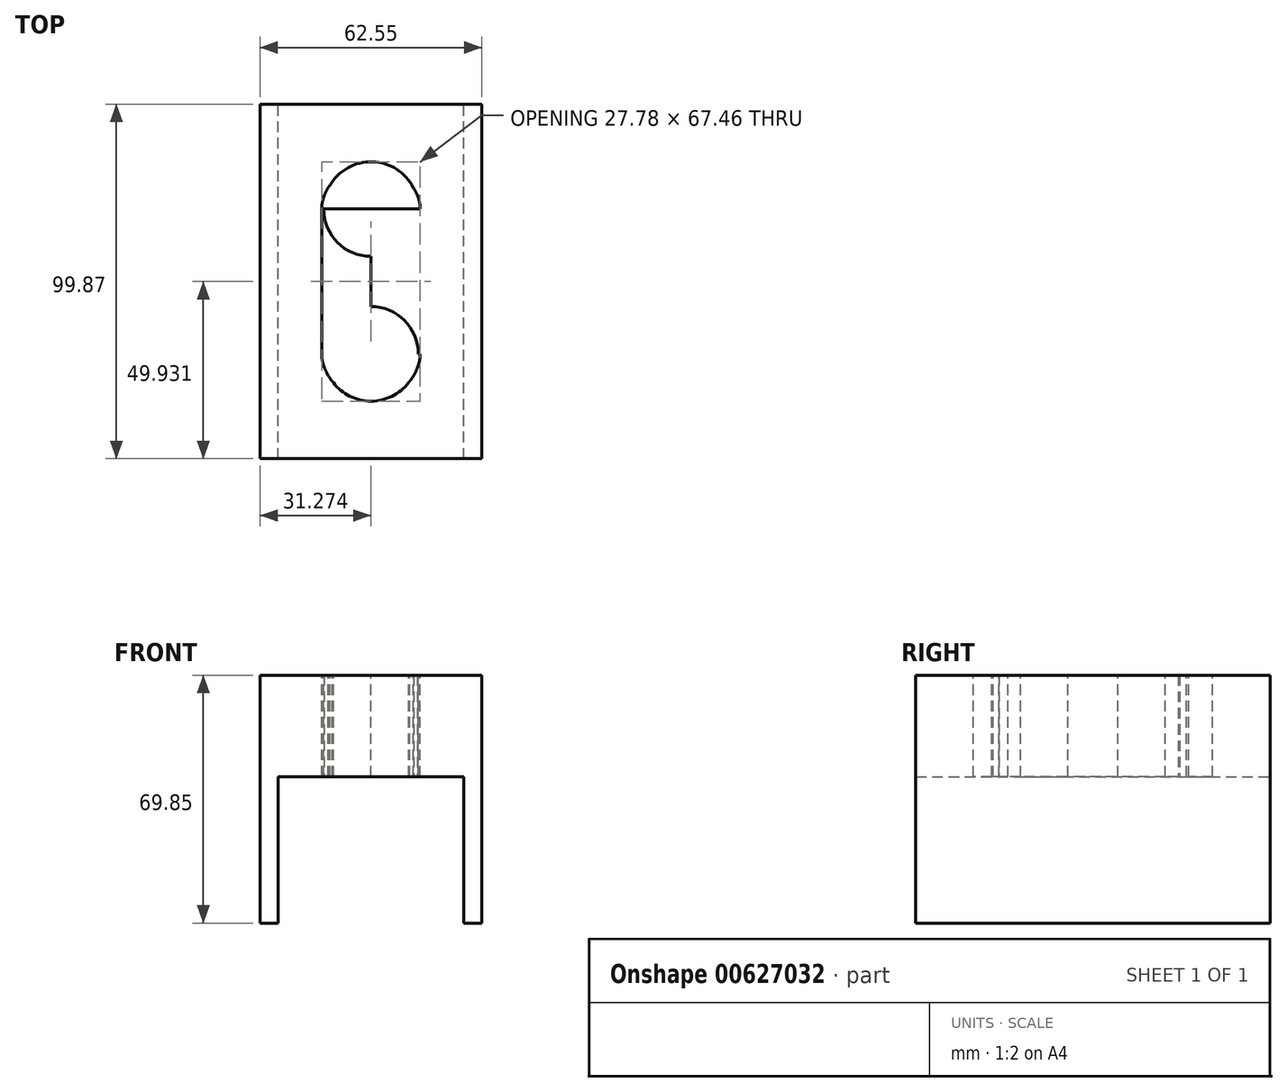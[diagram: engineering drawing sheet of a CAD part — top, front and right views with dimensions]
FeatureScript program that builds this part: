
annotation { "Feature Type Name" : "Feature", "Feature Type Description" : "" }
export const myFeature = defineFeature(function(context is Context, id is Id, definition is map)
    precondition{}
    {
        {
            var Q0;
            Q0=qCreatedBy(makeId("Front.planeOp"),FACE);
            var sketch = newSketch(context, id + "F0", { "sketchPlane" : qUnion([Q0])});
            skLineSegment(sketch, "E0", {"start": v(-13.71, -48.82) * mm, "end": v(-13.71, 21.03) * mm});
            skLineSegment(sketch, "E1", {"start": v(-13.71, 21.03) * mm, "end": v(48.84, 21.03) * mm});
            skLineSegment(sketch, "E2", {"start": v(48.84, 21.03) * mm, "end": v(48.84, -48.82) * mm});
            skLineSegment(sketch, "E3", {"start": v(-13.71, -48.82) * mm, "end": v(-8.63, -48.82) * mm});
            skLineSegment(sketch, "E4", {"start": v(-8.63, -48.82) * mm, "end": v(-8.63, -7.55) * mm});
            skLineSegment(sketch, "E5", {"start": v(-8.63, -7.55) * mm, "end": v(43.76, -7.55) * mm});
            skLineSegment(sketch, "E6", {"start": v(43.76, -7.55) * mm, "end": v(43.76, -48.82) * mm});
            skLineSegment(sketch, "E7", {"start": v(43.76, -48.82) * mm, "end": v(48.84, -48.82) * mm});
            skSolve(sketch);
        }
        {
            var Q0;
            Q0=makeQuery(id+"F0.imprint","IMPRINT",FACE,{"disambiguationData":[TD([[makeQuery(id+"F0.imprint","IMPRINT",EDGE,{"derivedFrom":sQuery(id+"F0.wireOp",EDGE,"E0")}),-1.0]])]});
            extrude(context, id + "F1", {"entities" : qUnion([Q0]), "depth" : 99.87 * mm, "offsetDistance" : 25.4 * mm});
        }
        {
            var Q0;
            Q0=makeQuery(id+"F1.opExtrude","SWEPT_FACE",FACE,{"disambiguationData":[OSD([sQuery(id+"F0.wireOp",EDGE,"E1")])]});
            var sketch = newSketch(context, id + "F2", { "sketchPlane" : qUnion([Q0])});
            skLineSegment(sketch, "E8", {"start": v(17.56, -49.94) * mm, "end": v(17.56, -29.54) * mm});
            skPoint(sketch, "E8.startSnap0", {"position": v(17.56, 0) * mm});
            skPoint(sketch, "E8.startSnap1", {"position": v(48.84, -49.94) * mm});
            skLineSegment(sketch, "E9", {"start": v(17.56, -49.94) * mm, "end": v(17.56, -70.34) * mm});
            skCircle(sketch, "E10", {"center": v(17.56, -70.34) * mm, "radius": 13.34 * mm});
            skLineSegment(sketch, "E11", {"start": v(17.56, -29.54) * mm, "end": v(3.67, -29.54) * mm});
            skLineSegment(sketch, "E12", {"start": v(17.56, -29.54) * mm, "end": v(31.45, -29.54) * mm});
            skLineSegment(sketch, "E13.MirrorCS", {"start": v(31.65, -49.94) * mm, "end": v(17.56, -49.94) * mm});
            skLineSegment(sketch, "E14.MirrorCS", {"start": v(17.56, -49.94) * mm, "end": v(17.56, -68.43) * mm});
            skLineSegment(sketch, "E15", {"start": v(17.56, -49.94) * mm, "end": v(17.56, -29.3) * mm});
            skLineSegment(sketch, "E16", {"start": v(31.45, -70.34) * mm, "end": v(31.45, -71.45) * mm});
            skLineSegment(sketch, "E17", {"start": v(17.56, -70.34) * mm, "end": v(31.45, -70.34) * mm});
            skLineSegment(sketch, "E18", {"start": v(31.45, -29.54) * mm, "end": v(31.45, -70.34) * mm});
            skLineSegment(sketch, "E19.MirrorCS", {"start": v(3.67, -29.54) * mm, "end": v(3.67, -70.34) * mm});
            skCircle(sketch, "E20.MirrorC", {"center": v(17.56, -29.54) * mm, "radius": 13.34 * mm});
            skArc(sketch, "E21", {"start": v(31.45, -29.54) * mm, "mid": v(30.95, -26.4) * mm, "end": v(29.5, -23.6) * mm});
            skFitSpline(sketch, "E22", {"points": [v(30.79, -25.94) * mm, v(29.14, -22.92) * mm, v(28.47, -22.99) * mm], "startDerivative": vector(-2.43, 5.95) * mm, "endDerivative": vector(-2.16, -0.91) * mm});
            skFitSpline(sketch, "E23", {"points": [v(29.58, -23.38) * mm, v(28.4, -21.78) * mm, v(28.32, -21.8) * mm], "startDerivative": vector(-1.8, 2.77) * mm, "endDerivative": vector(-0.4, -0.27) * mm});
            skFitSpline(sketch, "E24", {"points": [v(28.5, -21.84) * mm, v(28.17, -21.46) * mm, v(27.98, -21.27) * mm], "startDerivative": vector(-0.61, 0.7) * mm, "endDerivative": vector(-0.4, 0.44) * mm});
            skArc(sketch, "E25.MirrorCS", {"start": v(3.67, -29.54) * mm, "mid": v(4.17, -26.4) * mm, "end": v(5.63, -23.6) * mm});
            skFitSpline(sketch, "E26.MirrorCS", {"points": [v(4.34, -25.94) * mm, v(5.99, -22.92) * mm, v(6.66, -22.99) * mm], "startDerivative": vector(2.43, 5.95) * mm, "endDerivative": vector(2.16, -0.91) * mm});
            skFitSpline(sketch, "E27.MirrorCS", {"points": [v(5.54, -23.38) * mm, v(6.72, -21.78) * mm, v(6.8, -21.8) * mm], "startDerivative": vector(1.8, 2.77) * mm, "endDerivative": vector(0.4, -0.27) * mm});
            skFitSpline(sketch, "E28.MirrorCS", {"points": [v(6.63, -21.84) * mm, v(6.95, -21.46) * mm, v(7.15, -21.27) * mm], "startDerivative": vector(0.61, 0.7) * mm, "endDerivative": vector(0.4, 0.44) * mm});
            skArc(sketch, "E29.MirrorCS", {"start": v(31.45, -70.34) * mm, "mid": v(30.95, -73.46) * mm, "end": v(29.5, -76.28) * mm});
            skFitSpline(sketch, "E30.MirrorCS", {"points": [v(30.79, -73.93) * mm, v(29.14, -76.95) * mm, v(28.47, -76.89) * mm], "startDerivative": vector(-2.43, -5.95) * mm, "endDerivative": vector(-2.16, 0.91) * mm});
            skFitSpline(sketch, "E31.MirrorCS", {"points": [v(29.58, -76.5) * mm, v(28.4, -78.1) * mm, v(28.32, -78.07) * mm], "startDerivative": vector(-1.8, -2.77) * mm, "endDerivative": vector(-0.4, 0.27) * mm});
            skFitSpline(sketch, "E32.MirrorCS", {"points": [v(28.5, -78.04) * mm, v(28.17, -78.41) * mm, v(27.98, -78.6) * mm], "startDerivative": vector(-0.61, -0.7) * mm, "endDerivative": vector(-0.4, -0.44) * mm});
            skFitSpline(sketch, "E33.MirrorCS", {"points": [v(6.63, -78.04) * mm, v(6.95, -78.41) * mm, v(7.15, -78.6) * mm], "startDerivative": vector(0.61, -0.7) * mm, "endDerivative": vector(0.4, -0.44) * mm});
            skFitSpline(sketch, "E34.MirrorCS", {"points": [v(5.54, -76.5) * mm, v(6.72, -78.1) * mm, v(6.8, -78.07) * mm], "startDerivative": vector(1.8, -2.77) * mm, "endDerivative": vector(0.4, 0.27) * mm});
            skFitSpline(sketch, "E35.MirrorCS", {"points": [v(4.34, -73.93) * mm, v(5.99, -76.95) * mm, v(6.66, -76.89) * mm], "startDerivative": vector(2.43, -5.95) * mm, "endDerivative": vector(2.16, 0.91) * mm});
            skArc(sketch, "E36.MirrorCS", {"start": v(3.67, -70.34) * mm, "mid": v(4.17, -73.46) * mm, "end": v(5.63, -76.28) * mm});
            skSolve(sketch);
        }
        {
            var Q0;
            {var subQ0=sQuery(id+"F2.wireOp",EDGE,"E20.MirrorC");var subQ13=makeQuery(id+"F2.imprint","INTERSECT",VERTEX,{"derivedFrom":[subQ0,sQuery(id+"F2.wireOp",EDGE,"E25.MirrorCS")]});Q0=makeQuery(id+"F2.imprint","IMPRINT",FACE,{"disambiguationData":[TD([[makeQuery(id+"F2.imprint","IMPRINT",EDGE,{"disambiguationData":[TD([[subQ13,1.0]])],"derivedFrom":subQ0}),-1.0]])]});}
            var Q1;
            {var subQ0=sQuery(id+"F2.wireOp",EDGE,"E27.MirrorCS");var subQ1=sQuery(id+"F2.wireOp",EDGE,"E20.MirrorC");var subQ2=makeQuery(id+"F2.imprint","INTERSECT",VERTEX,{"derivedFrom":[subQ1,subQ0]});Q1=makeQuery(id+"F2.imprint","IMPRINT",FACE,{"disambiguationData":[TD([[makeQuery(id+"F2.imprint","IMPRINT",EDGE,{"disambiguationData":[TD([[subQ2,-1.0]])],"derivedFrom":subQ1}),1.0]])]});}
            var Q2;
            {var subQ0=sQuery(id+"F2.wireOp",EDGE,"E26.MirrorCS");var subQ1=sQuery(id+"F2.wireOp",EDGE,"E20.MirrorC");var subQ2=makeQuery(id+"F2.imprint","INTERSECT",VERTEX,{"derivedFrom":[subQ1,subQ0]});Q2=makeQuery(id+"F2.imprint","IMPRINT",FACE,{"disambiguationData":[TD([[makeQuery(id+"F2.imprint","IMPRINT",EDGE,{"disambiguationData":[TD([[subQ2,-1.0]])],"derivedFrom":subQ1}),1.0]])]});}
            var Q3;
            {var subQ0=sQuery(id+"F2.wireOp",EDGE,"E25.MirrorCS");var subQ1=sQuery(id+"F2.wireOp",EDGE,"E20.MirrorC");var subQ2=makeQuery(id+"F2.imprint","INTERSECT",VERTEX,{"derivedFrom":[subQ1,subQ0]});Q3=makeQuery(id+"F2.imprint","IMPRINT",FACE,{"disambiguationData":[TD([[makeQuery(id+"F2.imprint","IMPRINT",EDGE,{"disambiguationData":[TD([[subQ2,-1.0]])],"derivedFrom":subQ1}),1.0]])]});}
            var Q4;
            {var subQ0=sQuery(id+"F2.wireOp",EDGE,"E25.MirrorCS");var subQ5=sQuery(id+"F2.wireOp",EDGE,"E20.MirrorC");var subQ7=makeQuery(id+"F2.imprint","INTERSECT",VERTEX,{"derivedFrom":[subQ5,subQ0]});Q4=makeQuery(id+"F2.imprint","IMPRINT",FACE,{"disambiguationData":[TD([[makeQuery(id+"F2.imprint","IMPRINT",EDGE,{"disambiguationData":[TD([[subQ7,1.0]])],"derivedFrom":subQ5}),1.0]])]});}
            var Q5;
            {var subQ0=sQuery(id+"F2.wireOp",EDGE,"E24");var subQ1=sQuery(id+"F2.wireOp",EDGE,"E20.MirrorC");var subQ2=makeQuery(id+"F2.imprint","INTERSECT",VERTEX,{"derivedFrom":[subQ1,subQ0]});Q5=makeQuery(id+"F2.imprint","IMPRINT",FACE,{"disambiguationData":[TD([[makeQuery(id+"F2.imprint","IMPRINT",EDGE,{"disambiguationData":[TD([[subQ2,-1.0]])],"derivedFrom":subQ1}),1.0]])]});}
            var Q6;
            {var subQ0=sQuery(id+"F2.wireOp",EDGE,"E23");var subQ1=sQuery(id+"F2.wireOp",EDGE,"E20.MirrorC");var subQ2=makeQuery(id+"F2.imprint","INTERSECT",VERTEX,{"derivedFrom":[subQ1,subQ0]});Q6=makeQuery(id+"F2.imprint","IMPRINT",FACE,{"disambiguationData":[TD([[makeQuery(id+"F2.imprint","IMPRINT",EDGE,{"disambiguationData":[TD([[subQ2,-1.0]])],"derivedFrom":subQ1}),1.0]])]});}
            var Q7;
            {var subQ0=sQuery(id+"F2.wireOp",EDGE,"E21");var subQ1=sQuery(id+"F2.wireOp",EDGE,"E20.MirrorC");var subQ2=makeQuery(id+"F2.imprint","INTERSECT",VERTEX,{"derivedFrom":[subQ1,subQ0]});Q7=makeQuery(id+"F2.imprint","IMPRINT",FACE,{"disambiguationData":[TD([[makeQuery(id+"F2.imprint","IMPRINT",EDGE,{"disambiguationData":[TD([[subQ2,-1.0]])],"derivedFrom":subQ1}),1.0]])]});}
            var Q8;
            {var subQ0=sQuery(id+"F2.wireOp",EDGE,"E21");var subQ1=sQuery(id+"F2.wireOp",EDGE,"E20.MirrorC");var subQ2=makeQuery(id+"F2.imprint","INTERSECT",VERTEX,{"derivedFrom":[subQ1,subQ0]});Q8=makeQuery(id+"F2.imprint","IMPRINT",FACE,{"disambiguationData":[TD([[makeQuery(id+"F2.imprint","IMPRINT",EDGE,{"disambiguationData":[TD([[subQ2,1.0]])],"derivedFrom":subQ1}),1.0]])]});}
            var Q9;
            {var subQ1=sQuery(id+"F2.wireOp",EDGE,"E11");var subQ3=sQuery(id+"F2.wireOp",EDGE,"E20.MirrorC");var subQ4=makeQuery(id+"F2.imprint","INTERSECT",VERTEX,{"derivedFrom":[subQ1,subQ3]});Q9=makeQuery(id+"F2.imprint","IMPRINT",FACE,{"disambiguationData":[TD([[makeQuery(id+"F2.imprint","IMPRINT",EDGE,{"disambiguationData":[TD([[subQ4,1.0]])],"derivedFrom":subQ3}),-1.0]])]});}
            var Q10;
            {var subQ1=sQuery(id+"F2.wireOp",EDGE,"E12");var subQ3=sQuery(id+"F2.wireOp",EDGE,"E20.MirrorC");var subQ4=makeQuery(id+"F2.imprint","INTERSECT",VERTEX,{"derivedFrom":[subQ1,subQ3]});Q10=makeQuery(id+"F2.imprint","IMPRINT",FACE,{"disambiguationData":[TD([[makeQuery(id+"F2.imprint","IMPRINT",EDGE,{"disambiguationData":[TD([[subQ4,-1.0]])],"derivedFrom":subQ3}),-1.0]])]});}
            var Q11;
            {var subQ11=sQuery(id+"F2.wireOp",EDGE,"E19.MirrorCS");Q11=makeQuery(id+"F2.imprint","IMPRINT",FACE,{"disambiguationData":[TD([[makeQuery(id+"F2.imprint","IMPRINT",EDGE,{"derivedFrom":subQ11}),1.0]])]});}
            var Q12;
            {var subQ1=sQuery(id+"F2.wireOp",EDGE,"E12");var subQ7=sQuery(id+"F2.wireOp",EDGE,"E20.MirrorC");var subQ9=makeQuery(id+"F2.imprint","INTERSECT",VERTEX,{"derivedFrom":[subQ1,subQ7]});Q12=makeQuery(id+"F2.imprint","IMPRINT",FACE,{"disambiguationData":[TD([[makeQuery(id+"F2.imprint","IMPRINT",EDGE,{"disambiguationData":[TD([[subQ9,-1.0]])],"derivedFrom":subQ7}),1.0]])]});}
            var Q13;
            {var subQ0=sQuery(id+"F2.wireOp",EDGE,"E14.MirrorCS");var subQ7=sQuery(id+"F2.wireOp",EDGE,"E10");var subQ9=makeQuery(id+"F2.imprint","INTERSECT",VERTEX,{"derivedFrom":[subQ7,subQ0]});Q13=makeQuery(id+"F2.imprint","IMPRINT",FACE,{"disambiguationData":[TD([[makeQuery(id+"F2.imprint","IMPRINT",EDGE,{"disambiguationData":[TD([[subQ9,1.0]])],"derivedFrom":subQ7}),-1.0]])]});}
            var Q14;
            {var subQ9=sQuery(id+"F2.wireOp",EDGE,"E9");Q14=makeQuery(id+"F2.imprint","IMPRINT",FACE,{"disambiguationData":[TD([[makeQuery(id+"F2.imprint","IMPRINT",EDGE,{"derivedFrom":subQ9}),-1.0]])]});}
            var Q15;
            {var subQ0=sQuery(id+"F2.wireOp",EDGE,"E9");Q15=makeQuery(id+"F2.imprint","IMPRINT",FACE,{"disambiguationData":[TD([[makeQuery(id+"F2.imprint","IMPRINT",EDGE,{"derivedFrom":subQ0}),1.0]])]});}
            var Q16;
            {var subQ0=sQuery(id+"F2.wireOp",EDGE,"E29.MirrorCS");var subQ5=sQuery(id+"F2.wireOp",EDGE,"E10");var subQ7=makeQuery(id+"F2.imprint","INTERSECT",VERTEX,{"derivedFrom":[subQ5,subQ0]});Q16=makeQuery(id+"F2.imprint","IMPRINT",FACE,{"disambiguationData":[TD([[makeQuery(id+"F2.imprint","IMPRINT",EDGE,{"disambiguationData":[TD([[subQ7,-1.0]])],"derivedFrom":subQ5}),-1.0]])]});}
            var Q17;
            {var subQ0=sQuery(id+"F2.wireOp",EDGE,"E29.MirrorCS");var subQ1=sQuery(id+"F2.wireOp",EDGE,"E10");var subQ2=makeQuery(id+"F2.imprint","INTERSECT",VERTEX,{"derivedFrom":[subQ1,subQ0]});Q17=makeQuery(id+"F2.imprint","IMPRINT",FACE,{"disambiguationData":[TD([[makeQuery(id+"F2.imprint","IMPRINT",EDGE,{"disambiguationData":[TD([[subQ2,1.0]])],"derivedFrom":subQ1}),-1.0]])]});}
            var Q18;
            {var subQ0=sQuery(id+"F2.wireOp",EDGE,"E31.MirrorCS");var subQ1=sQuery(id+"F2.wireOp",EDGE,"E10");var subQ2=makeQuery(id+"F2.imprint","INTERSECT",VERTEX,{"derivedFrom":[subQ1,subQ0]});Q18=makeQuery(id+"F2.imprint","IMPRINT",FACE,{"disambiguationData":[TD([[makeQuery(id+"F2.imprint","IMPRINT",EDGE,{"disambiguationData":[TD([[subQ2,-1.0]])],"derivedFrom":subQ1}),-1.0]])]});}
            var Q19;
            {var subQ0=sQuery(id+"F2.wireOp",EDGE,"E36.MirrorCS");var subQ1=sQuery(id+"F2.wireOp",EDGE,"E10");var subQ2=makeQuery(id+"F2.imprint","INTERSECT",VERTEX,{"derivedFrom":[subQ1,subQ0]});Q19=makeQuery(id+"F2.imprint","IMPRINT",FACE,{"disambiguationData":[TD([[makeQuery(id+"F2.imprint","IMPRINT",EDGE,{"disambiguationData":[TD([[subQ2,-1.0]])],"derivedFrom":subQ1}),-1.0]])]});}
            var Q20;
            {var subQ0=sQuery(id+"F2.wireOp",EDGE,"E35.MirrorCS");var subQ1=sQuery(id+"F2.wireOp",EDGE,"E10");var subQ2=makeQuery(id+"F2.imprint","INTERSECT",VERTEX,{"derivedFrom":[subQ1,subQ0]});Q20=makeQuery(id+"F2.imprint","IMPRINT",FACE,{"disambiguationData":[TD([[makeQuery(id+"F2.imprint","IMPRINT",EDGE,{"disambiguationData":[TD([[subQ2,-1.0]])],"derivedFrom":subQ1}),-1.0]])]});}
            extrude(context, id + "F3", {"entities" : qUnion([Q0, Q1, Q2, Q3, Q4, Q5, Q6, Q7, Q8, Q9, Q10, Q11, Q12, Q13, Q14, Q15, Q16, Q17, Q18, Q19, Q20]), "operationType" : NewBodyOperationType.REMOVE, "oppositeDirection" : true, "depth" : 76.2 * mm, "offsetDistance" : 25.4 * mm});
        }
    });
